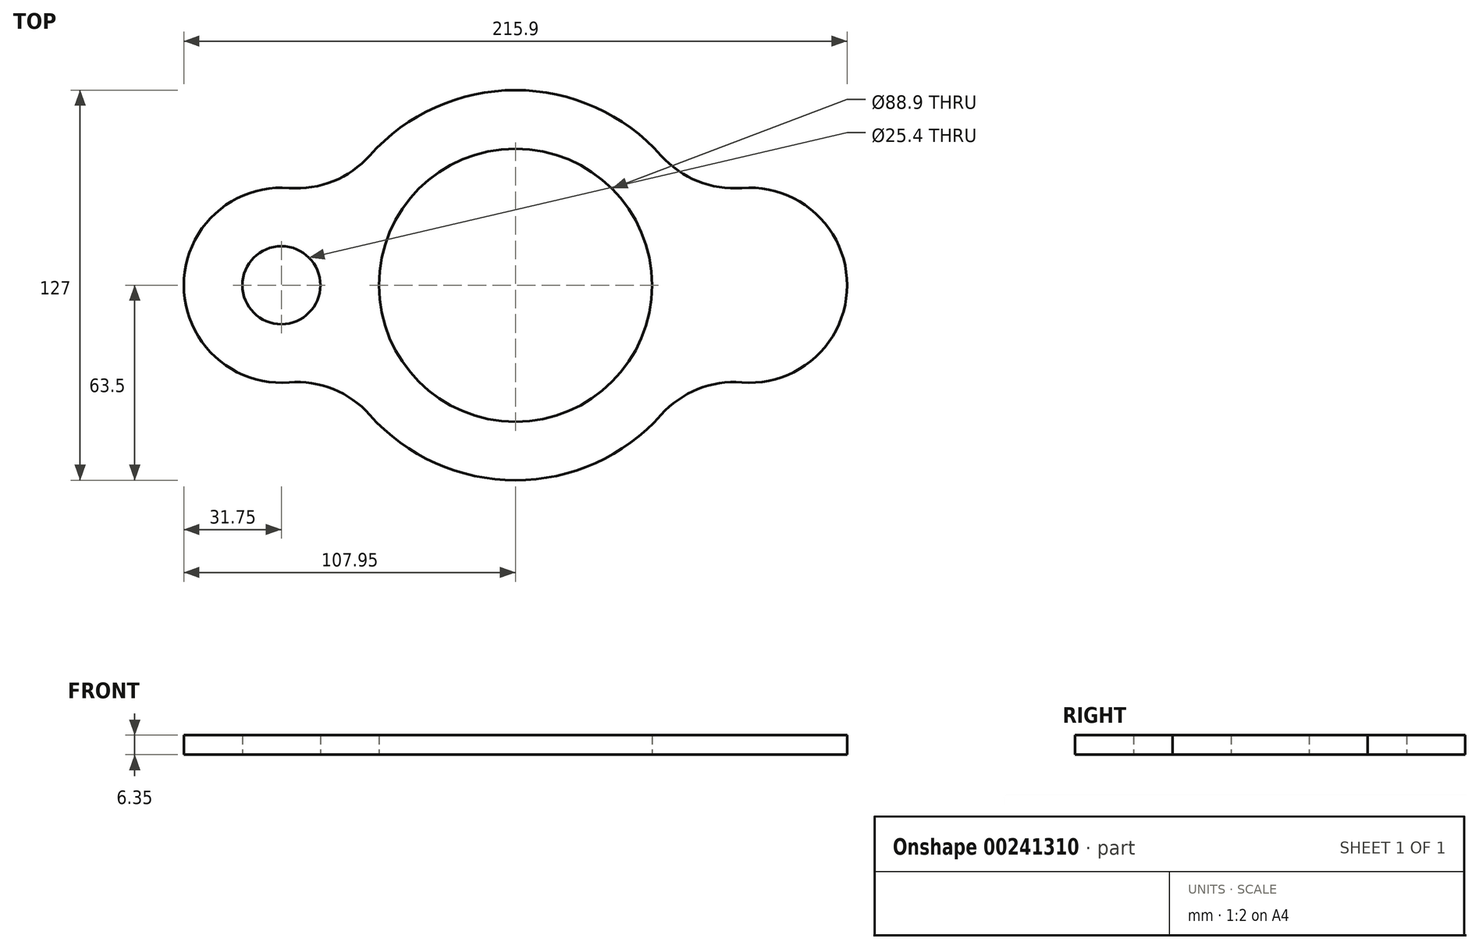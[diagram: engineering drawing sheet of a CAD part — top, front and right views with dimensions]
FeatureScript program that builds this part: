
annotation { "Feature Type Name" : "Feature", "Feature Type Description" : "" }
export const myFeature = defineFeature(function(context is Context, id is Id, definition is map)
    precondition{}
    {
        {
            var Q0;
            Q0=qCreatedBy(makeId("Top.planeOp"),FACE);
            var sketch = newSketch(context, id + "F0", { "sketchPlane" : qUnion([Q0])});
            skCircle(sketch, "E0", {"center": v(0, 0) * mm, "radius": 44.45 * mm});
            skArc(sketch, "E1", {"start": v(-57.94, -25.98) * mm, "mid": v(0, -63.5) * mm, "end": v(57.94, -25.98) * mm});
            skLineSegment(sketch, "E2", {"start": v(0, 0) * mm, "end": v(-76.2, 0) * mm, "construction": true});
            skCircle(sketch, "E3", {"center": v(-76.2, 0) * mm, "radius": 12.7 * mm});
            skLineSegment(sketch, "E4", {"start": v(0, 0) * mm, "end": v(0, -44.45) * mm, "construction": true});
            skArc(sketch, "E5", {"start": v(-57.94, 25.98) * mm, "mid": v(-107.95, 0) * mm, "end": v(-57.94, -25.98) * mm});
            skArc(sketch, "E6.MirrorC", {"start": v(57.94, 25.98) * mm, "mid": v(107.95, 0) * mm, "end": v(57.94, -25.98) * mm});
            skCircle(sketch, "E7.MirrorC", {"center": v(76.2, 0) * mm, "radius": 12.7 * mm});
            skArc(sketch, "E8.trimOffspring", {"start": v(57.94, 25.98) * mm, "mid": v(0, 63.5) * mm, "end": v(-57.94, 25.98) * mm});
            skSolve(sketch);
        }
        {
            var Q0;
            {var subQ0=sQuery(id+"F0.wireOp",EDGE,"E5");var subQ1=sQuery(id+"F0.wireOp",EDGE,"E0");var subQ2=makeQuery(id+"F0.imprint","INTERSECT",VERTEX,{"derivedFrom":[subQ1,subQ0]});Q0=makeQuery(id+"F0.imprint","IMPRINT",FACE,{"disambiguationData":[TD([[makeQuery(id+"F0.imprint","IMPRINT",EDGE,{"disambiguationData":[TD([[subQ2,1.0]])],"derivedFrom":subQ1}),-1.0]])]});}
            var Q1;
            {var subQ0=sQuery(id+"F0.wireOp",EDGE,"E5");var subQ1=sQuery(id+"F0.wireOp",EDGE,"E1");var subQ2=makeQuery(id+"F0.imprint","INTERSECT",VERTEX,{"disambiguationData":[OD(0.0)],"derivedFrom":[subQ1,subQ0]});Q1=makeQuery(id+"F0.imprint","IMPRINT",FACE,{"disambiguationData":[TD([[makeQuery(id+"F0.imprint","IMPRINT",EDGE,{"disambiguationData":[TD([[subQ2,-1.0]])],"derivedFrom":subQ1}),1.0]])]});}
            var Q2;
            {var subQ3=sQuery(id+"F0.wireOp",EDGE,"E3");Q2=makeQuery(id+"F0.imprint","IMPRINT",FACE,{"disambiguationData":[TD([[makeQuery(id+"F0.imprint","IMPRINT",EDGE,{"derivedFrom":subQ3}),-1.0]])]});}
            var Q3;
            {var subQ0=sQuery(id+"F0.wireOp",EDGE,"E5");var subQ1=sQuery(id+"F0.wireOp",EDGE,"E0");var subQ2=makeQuery(id+"F0.imprint","INTERSECT",VERTEX,{"derivedFrom":[subQ1,subQ0]});Q3=makeQuery(id+"F0.imprint","IMPRINT",FACE,{"disambiguationData":[TD([[makeQuery(id+"F0.imprint","IMPRINT",EDGE,{"disambiguationData":[TD([[subQ2,-1.0]])],"derivedFrom":subQ1}),-1.0]])]});}
            var Q4;
            {var subQ3=sQuery(id+"F0.wireOp",EDGE,"E7.MirrorC");Q4=makeQuery(id+"F0.imprint","IMPRINT",FACE,{"disambiguationData":[TD([[makeQuery(id+"F0.imprint","IMPRINT",EDGE,{"derivedFrom":subQ3}),1.0]])]});}
            var Q5;
            {var subQ0=sQuery(id+"F0.wireOp",EDGE,"E6.MirrorC");var subQ1=sQuery(id+"F0.wireOp",EDGE,"E1");var subQ2=makeQuery(id+"F0.imprint","INTERSECT",VERTEX,{"disambiguationData":[OD(0.0)],"derivedFrom":[subQ1,subQ0]});Q5=makeQuery(id+"F0.imprint","IMPRINT",FACE,{"disambiguationData":[TD([[makeQuery(id+"F0.imprint","IMPRINT",EDGE,{"disambiguationData":[TD([[subQ2,1.0]])],"derivedFrom":subQ1}),1.0]])]});}
            extrude(context, id + "F1", {"entities" : qUnion([Q0, Q1, Q2, Q3, Q4, Q5]), "depth" : 6.35 * mm});
        }
        {
            var Q0;
            {var subQ0=sQuery(id+"F0.wireOp",EDGE,"E5");var subQ1=sQuery(id+"F0.wireOp",EDGE,"E1");Q0=makeQuery(id+"F1.opExtrude","SWEPT_EDGE",EDGE,{"disambiguationData":[OSD([subQ1,subQ0]),TDD([makeQuery(id+"F0.imprint","INTERSECT",VERTEX,{"disambiguationData":[OD(1.0)],"derivedFrom":[subQ1,subQ0]})])]});}
            var Q1;
            {var subQ0=sQuery(id+"F0.wireOp",EDGE,"E6.MirrorC");var subQ1=sQuery(id+"F0.wireOp",EDGE,"E1");Q1=makeQuery(id+"F1.opExtrude","SWEPT_EDGE",EDGE,{"disambiguationData":[OSD([subQ1,subQ0]),TDD([makeQuery(id+"F0.imprint","INTERSECT",VERTEX,{"disambiguationData":[OD(1.0)],"derivedFrom":[subQ1,subQ0]})])]});}
            var Q2;
            {var subQ0=sQuery(id+"F0.wireOp",EDGE,"E6.MirrorC");var subQ1=sQuery(id+"F0.wireOp",EDGE,"E1");Q2=makeQuery(id+"F1.opExtrude","SWEPT_EDGE",EDGE,{"disambiguationData":[OSD([subQ1,subQ0]),TDD([makeQuery(id+"F0.imprint","INTERSECT",VERTEX,{"disambiguationData":[OD(0.0)],"derivedFrom":[subQ1,subQ0]})])]});}
            var Q3;
            {var subQ0=sQuery(id+"F0.wireOp",EDGE,"E5");var subQ1=sQuery(id+"F0.wireOp",EDGE,"E1");Q3=makeQuery(id+"F1.opExtrude","SWEPT_EDGE",EDGE,{"disambiguationData":[OSD([subQ1,subQ0]),TDD([makeQuery(id+"F0.imprint","INTERSECT",VERTEX,{"disambiguationData":[OD(0.0)],"derivedFrom":[subQ1,subQ0]})])]});}
            var Q4;
            Q4=makeQuery(id+"F1.opExtrude","SWEPT_EDGE",EDGE,{"disambiguationData":[OSD([sQuery(id+"F0.wireOp",EDGE,"E5"),sQuery(id+"F0.wireOp",EDGE,"E8.trimOffspring")])]});
            var Q5;
            Q5=makeQuery(id+"F1.opExtrude","SWEPT_EDGE",EDGE,{"disambiguationData":[OSD([sQuery(id+"F0.wireOp",EDGE,"E6.MirrorC"),sQuery(id+"F0.wireOp",EDGE,"E8.trimOffspring")])]});
            fillet(context, id + "F2", {"entities" : qUnion([Q0, Q1, Q2, Q3, Q4, Q5]), "radius" : 31.75 * mm, "tangentPropagation" : true, "allowEdgeOverflow" : false});
        }
    });
